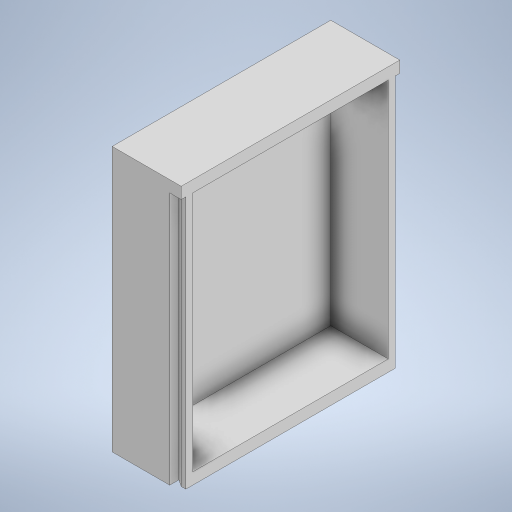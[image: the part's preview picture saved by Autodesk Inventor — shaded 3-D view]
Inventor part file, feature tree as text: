
AUTODESK INVENTOR PART (.ipt)
format: ipt  version: 2024.3 (Build 283343000, 343)  size: 235,520 bytes
history: native  units: mm
features: extrude x3, sketch x2, other x1
ambient origin geometry x8: Origin, YZ Plane, XZ Plane, XY Plane, X Axis, Y Axis, Z Axis, Center Point
bodies: Body1 (feature_tree)
feature tree (6):
  other  "Sólido1"
  sketch  "Boceto1"  dims[d0=85.0mm d1=105.0mm]
  extrude  "Extrusión1"  Depth=105.0mm
  extrude  "Extrusión2"  Depth=5.0mm
  extrude  "Extrusión3"  Depth=5.0mm
  sketch  "Boceto2"  dims[d2=5.0mm d3=5.0mm d4=5.0mm d5=5.0mm d6=30.0mm d7=0.0mm d8=5.0mm d9=0.0mm d10=2.0mm d11=2.0mm d12=4.0mm d13=5.0mm d14=0.0mm d15=110.0mm d16=0.0mm d17=0.0mm d18=0.0mm d19=0.0mm d20=0.0mm]
